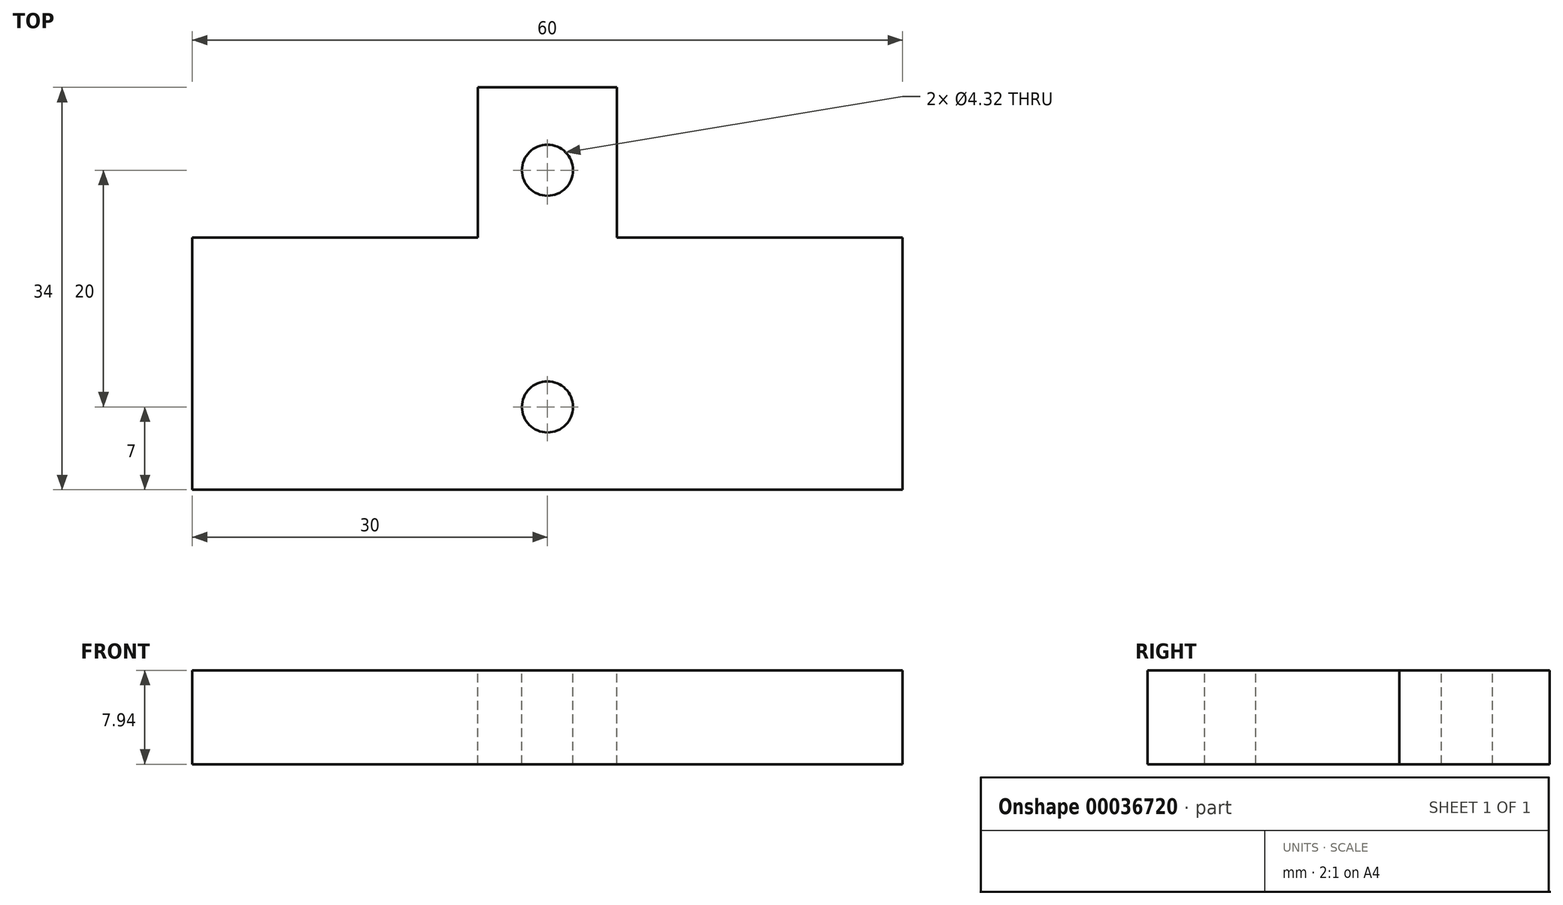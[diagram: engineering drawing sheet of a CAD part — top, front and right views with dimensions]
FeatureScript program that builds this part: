
annotation { "Feature Type Name" : "Feature", "Feature Type Description" : "" }
export const myFeature = defineFeature(function(context is Context, id is Id, definition is map)
    precondition{}
    {
        {
            var Q0;
            Q0=qCreatedBy(makeId("Top.planeOp"),FACE);
            var sketch = newSketch(context, id + "F0", { "sketchPlane" : qUnion([Q0])});
            skLineSegment(sketch, "E0.bottom", {"start": v(30, 17) * mm, "end": v(-30, 17) * mm});
            skLineSegment(sketch, "E0.top", {"start": v(30, -17) * mm, "end": v(-30, -17) * mm});
            skLineSegment(sketch, "E0.left", {"start": v(30, 17) * mm, "end": v(30, -17) * mm});
            skLineSegment(sketch, "E0.right", {"start": v(-30, 17) * mm, "end": v(-30, -17) * mm});
            skPoint(sketch, "E0.middle", {"position": v(0, 0) * mm});
            skSolve(sketch);
        }
        {
            var Q0;
            Q0=makeQuery(id+"F0.imprint","IMPRINT",FACE,{"disambiguationData":[TD([[makeQuery(id+"F0.imprint","IMPRINT",EDGE,{"derivedFrom":sQuery(id+"F0.wireOp",EDGE,"E0.bottom")}),1.0]])]});
            extrude(context, id + "F1", {"entities" : qUnion([Q0]), "depth" : 7.94 * mm, "offsetDistance" : 25.4 * mm});
        }
        {
            var Q0;
            Q0=makeQuery(id+"F1.opExtrude","CAP_FACE",FACE,{"disambiguationData":[OSD([sQuery(id+"F0.wireOp",EDGE,"E0.bottom"),sQuery(id+"F0.wireOp",EDGE,"E0.top"),sQuery(id+"F0.wireOp",EDGE,"E0.left"),sQuery(id+"F0.wireOp",EDGE,"E0.right")])],"isStart":false});
            var sketch = newSketch(context, id + "F2", { "sketchPlane" : qUnion([Q0])});
            skPoint(sketch, "E1.centerSnap0", {"position": v(0, 17) * mm});
            skPoint(sketch, "E2", {"position": v(0, 10) * mm});
            skPoint(sketch, "E3", {"position": v(0, -10) * mm});
            skSolve(sketch);
        }
        {
            var Q0;
            Q0=sQuery(id+"F2.wireOp",VERTEX,"E2");
            var Q1;
            Q1=sQuery(id+"F2.wireOp",VERTEX,"E3");
            var Q2;
            Q2=makeQuery(id+"F1.opExtrude","SWEPT_BODY",BODY,{"disambiguationData":[OSD([sQuery(id+"F0.wireOp",EDGE,"E0.bottom"),sQuery(id+"F0.wireOp",EDGE,"E0.top"),sQuery(id+"F0.wireOp",EDGE,"E0.left"),sQuery(id+"F0.wireOp",EDGE,"E0.right")])]});
            hole(context, id + "F3", {"style" : HoleStyle.SIMPLE, "endStyle" : HoleEndStyle.THROUGH, "standardTappedOrClearance" : lookupTablePath({ "fit" : "Normal (ASME)", "standard" : "ANSI", "size" : "#6", "type" : "Clearance" }), "standardBlindInLast" : lookupTablePath({ "fit" : "Normal", "standard" : "ANSI", "size" : "#6", "type" : "Clearance" }), "holeDiameter" : 4.32 * mm, "majorDiameter" : 3.5 * mm, "isTappedThrough" : true, "tappedDepth" : 10.3 * mm, "tapClearance" : 3, "locations" : qUnion([Q0, Q1]), "scope" : qUnion([Q2])});
        }
        {
            var Q0;
            Q0=makeQuery(id+"F1.opExtrude","CAP_FACE",FACE,{"disambiguationData":[OSD([sQuery(id+"F0.wireOp",EDGE,"E0.bottom"),sQuery(id+"F0.wireOp",EDGE,"E0.top"),sQuery(id+"F0.wireOp",EDGE,"E0.left"),sQuery(id+"F0.wireOp",EDGE,"E0.right")])],"isStart":false});
            var sketch = newSketch(context, id + "F4", { "sketchPlane" : qUnion([Q0])});
            skLineSegment(sketch, "E4.bottom", {"start": v(-30, 17) * mm, "end": v(-5.87, 17) * mm});
            skLineSegment(sketch, "E4.top", {"start": v(-30, 4.3) * mm, "end": v(-5.87, 4.3) * mm});
            skLineSegment(sketch, "E4.left", {"start": v(-30, 17) * mm, "end": v(-30, 4.3) * mm});
            skLineSegment(sketch, "E4.right", {"start": v(-5.87, 17) * mm, "end": v(-5.87, 4.3) * mm});
            skLineSegment(sketch, "E5.bottom", {"start": v(30, 17) * mm, "end": v(5.87, 17) * mm});
            skLineSegment(sketch, "E5.top", {"start": v(30, 4.3) * mm, "end": v(5.87, 4.3) * mm});
            skLineSegment(sketch, "E5.left", {"start": v(30, 17) * mm, "end": v(30, 4.3) * mm});
            skLineSegment(sketch, "E5.right", {"start": v(5.87, 17) * mm, "end": v(5.87, 4.3) * mm});
            skSolve(sketch);
        }
        {
            var Q0;
            Q0 = qSketchRegion(id + "F4", true);
            extrude(context, id + "F5", {"entities" : qUnion([Q0]), "operationType" : NewBodyOperationType.REMOVE, "endBound" : BoundingType.THROUGH_ALL, "oppositeDirection" : true, "depth" : 25.4 * mm, "offsetDistance" : 25.4 * mm});
        }
    });
